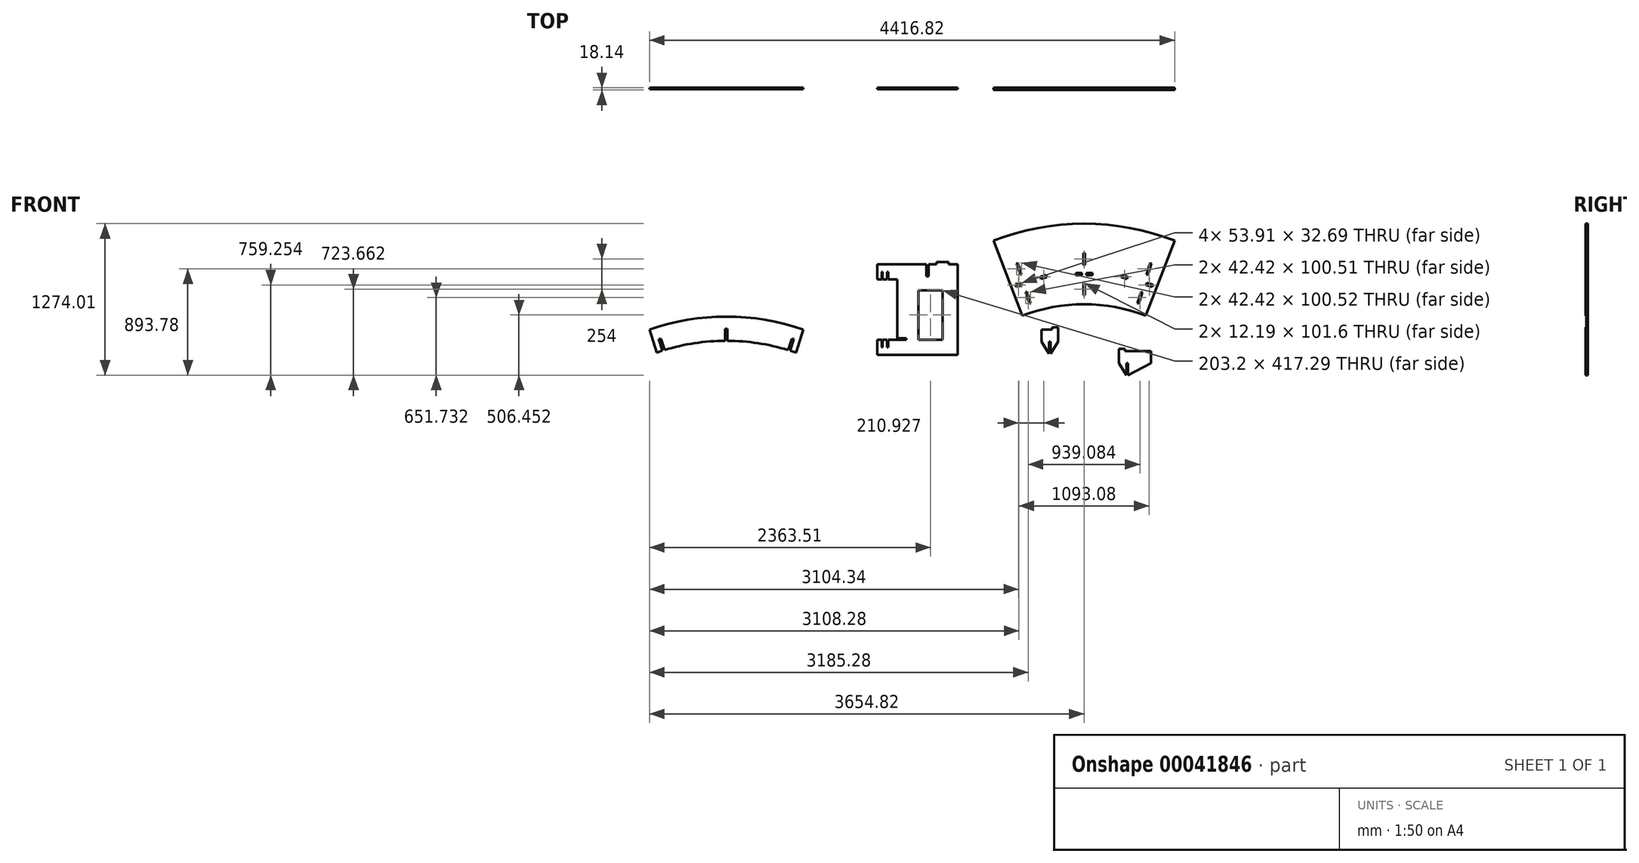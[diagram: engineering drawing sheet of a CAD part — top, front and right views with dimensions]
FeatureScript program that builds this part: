
annotation { "Feature Type Name" : "Feature", "Feature Type Description" : "" }
export const myFeature = defineFeature(function(context is Context, id is Id, definition is map)
    precondition{}
    {
        {
            var Q0;
            Q0=qCreatedBy(makeId("Front.planeOp"),FACE);
            var sketch = newSketch(context, id + "F0", { "sketchPlane" : qUnion([Q0])});
            skArc(sketch, "E0", {"start": v(822.71, 0) * mm, "mid": v(60.71, 141.8) * mm, "end": v(-701.29, 0) * mm});
            skArc(sketch, "E1.0", {"start": v(579.07, -632) * mm, "mid": v(60.71, -535.54) * mm, "end": v(-457.65, -632) * mm});
            skLineSegment(sketch, "E2", {"start": v(-701.29, 0) * mm, "end": v(-457.65, -632) * mm});
            skLineSegment(sketch, "E3", {"start": v(579.07, -632) * mm, "end": v(822.71, 0) * mm});
            skLineSegment(sketch, "E4.bottom", {"start": v(-1510, -199.4) * mm, "end": v(-1002, -199.4) * mm});
            skLineSegment(sketch, "E4.top", {"start": v(-1510, -961.4) * mm, "end": v(-1002, -961.4) * mm});
            skLineSegment(sketch, "E4.left", {"start": v(-1510, -326.4) * mm, "end": v(-1510, -822.2) * mm});
            skLineSegment(sketch, "E4.right", {"start": v(-1002, -199.4) * mm, "end": v(-1002, -961.4) * mm});
            skLineSegment(sketch, "E5.bottom", {"start": v(-1510, -199.4) * mm, "end": v(-1679.33, -199.4) * mm});
            skLineSegment(sketch, "E5.top", {"start": v(-1510, -326.4) * mm, "end": v(-1585.35, -326.4) * mm});
            skLineSegment(sketch, "E5.right", {"start": v(-1679.33, -199.4) * mm, "end": v(-1679.33, -326.4) * mm});
            skLineSegment(sketch, "E6", {"start": v(-1510, -580.4) * mm, "end": v(-1002, -580.4) * mm, "construction": true});
            skLineSegment(sketch, "E7", {"start": v(-1679.33, -262.9) * mm, "end": v(-1641.23, -262.9) * mm, "construction": true});
            skLineSegment(sketch, "E8.top", {"start": v(-1641.23, -262.9) * mm, "end": v(-1632.34, -262.9) * mm});
            skLineSegment(sketch, "E8.left", {"start": v(-1641.23, -326.4) * mm, "end": v(-1641.23, -262.9) * mm});
            skLineSegment(sketch, "E8.right", {"start": v(-1632.34, -326.4) * mm, "end": v(-1632.34, -262.9) * mm});
            skLineSegment(sketch, "E9", {"start": v(-1632.34, -262.9) * mm, "end": v(-1594.24, -262.9) * mm, "construction": true});
            skLineSegment(sketch, "E10.top", {"start": v(-1594.24, -262.9) * mm, "end": v(-1585.35, -262.9) * mm});
            skLineSegment(sketch, "E10.left", {"start": v(-1594.24, -326.4) * mm, "end": v(-1594.24, -262.9) * mm});
            skLineSegment(sketch, "E10.right", {"start": v(-1585.35, -326.4) * mm, "end": v(-1585.35, -262.9) * mm});
            skLineSegment(sketch, "E11.trimOffspring", {"start": v(-1641.23, -326.4) * mm, "end": v(-1679.33, -326.4) * mm});
            skLineSegment(sketch, "E12.trimOffspring", {"start": v(-1594.24, -326.4) * mm, "end": v(-1632.34, -326.4) * mm});
            skLineSegment(sketch, "E13.MirrorCS", {"start": v(-1641.23, -834.4) * mm, "end": v(-1679.33, -834.4) * mm});
            skLineSegment(sketch, "E14.MirrorCS", {"start": v(-1510, -834.4) * mm, "end": v(-1585.35, -834.4) * mm});
            skLineSegment(sketch, "E15.MirrorCS", {"start": v(-1632.34, -897.9) * mm, "end": v(-1594.24, -897.9) * mm, "construction": true});
            skLineSegment(sketch, "E16.MirrorCS", {"start": v(-1679.33, -897.9) * mm, "end": v(-1641.23, -897.9) * mm, "construction": true});
            skLineSegment(sketch, "E17.MirrorCS", {"start": v(-1594.24, -834.4) * mm, "end": v(-1594.24, -897.9) * mm});
            skLineSegment(sketch, "E18.MirrorCS", {"start": v(-1594.24, -834.4) * mm, "end": v(-1632.34, -834.4) * mm});
            skLineSegment(sketch, "E19.MirrorCS", {"start": v(-1679.33, -961.4) * mm, "end": v(-1679.33, -834.4) * mm});
            skLineSegment(sketch, "E20.MirrorCS", {"start": v(-1632.34, -834.4) * mm, "end": v(-1632.34, -897.9) * mm});
            skLineSegment(sketch, "E21.MirrorCS", {"start": v(-1641.23, -834.4) * mm, "end": v(-1641.23, -897.9) * mm});
            skLineSegment(sketch, "E22.MirrorCS", {"start": v(-1510, -961.4) * mm, "end": v(-1679.33, -961.4) * mm});
            skLineSegment(sketch, "E23.MirrorCS", {"start": v(-1641.23, -897.9) * mm, "end": v(-1632.34, -897.9) * mm});
            skLineSegment(sketch, "E24.MirrorCS", {"start": v(-1594.24, -897.9) * mm, "end": v(-1585.35, -897.9) * mm});
            skLineSegment(sketch, "E25.MirrorCS", {"start": v(-1585.35, -834.4) * mm, "end": v(-1585.35, -897.9) * mm});
            skLineSegment(sketch, "E26", {"start": v(-376.14, -603.35) * mm, "end": v(-581.47, 42.11) * mm, "construction": true});
            skLineSegment(sketch, "E27", {"start": v(60.71, -1976.58) * mm, "end": v(60.71, 636.15) * mm, "construction": true});
            skLineSegment(sketch, "E28", {"start": v(-476.24, -288.69) * mm, "end": v(-464.62, -285) * mm});
            skLineSegment(sketch, "E29", {"start": v(-464.62, -285) * mm, "end": v(-495.42, -188.17) * mm});
            skLineSegment(sketch, "E30", {"start": v(-495.42, -188.17) * mm, "end": v(-507.04, -191.87) * mm});
            skLineSegment(sketch, "E31", {"start": v(-507.04, -191.87) * mm, "end": v(-476.24, -288.69) * mm});
            skLineSegment(sketch, "E32.bottom", {"start": v(-1433.8, -199.4) * mm, "end": v(-1332.2, -199.4) * mm});
            skLineSegment(sketch, "E32.top", {"start": v(-1433.8, -181.26) * mm, "end": v(-1332.2, -181.26) * mm});
            skLineSegment(sketch, "E32.left", {"start": v(-1433.8, -199.4) * mm, "end": v(-1433.8, -181.26) * mm});
            skLineSegment(sketch, "E32.right", {"start": v(-1332.2, -199.4) * mm, "end": v(-1332.2, -181.26) * mm});
            skLineSegment(sketch, "E33", {"start": v(-1256, -199.4) * mm, "end": v(-1256, -961.4) * mm, "construction": true});
            skLineSegment(sketch, "E34.MirrorCS", {"start": v(-1078.2, -199.4) * mm, "end": v(-1078.2, -181.26) * mm});
            skLineSegment(sketch, "E35.MirrorCS", {"start": v(-1078.2, -199.4) * mm, "end": v(-1179.8, -199.4) * mm});
            skLineSegment(sketch, "E36.MirrorCS", {"start": v(-1179.8, -199.4) * mm, "end": v(-1179.8, -181.26) * mm});
            skLineSegment(sketch, "E37.MirrorCS", {"start": v(-1078.2, -181.26) * mm, "end": v(-1179.8, -181.26) * mm});
            skLineSegment(sketch, "E38.bottom", {"start": v(54.62, -103.75) * mm, "end": v(66.8, -103.75) * mm});
            skLineSegment(sketch, "E38.top", {"start": v(54.62, -205.35) * mm, "end": v(66.8, -205.35) * mm});
            skLineSegment(sketch, "E38.left", {"start": v(54.62, -103.75) * mm, "end": v(54.62, -205.35) * mm});
            skLineSegment(sketch, "E38.right", {"start": v(66.8, -103.75) * mm, "end": v(66.8, -205.35) * mm});
            skPoint(sketch, "E39", {"position": v(60.71, -103.75) * mm});
            skLineSegment(sketch, "E40", {"start": v(48.74, -281.55) * mm, "end": v(75.4, -281.55) * mm, "construction": true});
            skPoint(sketch, "E41.MirrorP", {"position": v(60.71, -459.35) * mm});
            skLineSegment(sketch, "E42.MirrorCS", {"start": v(54.62, -459.35) * mm, "end": v(66.8, -459.35) * mm});
            skLineSegment(sketch, "E43.MirrorCS", {"start": v(54.62, -459.35) * mm, "end": v(54.62, -357.75) * mm});
            skLineSegment(sketch, "E44.MirrorCS", {"start": v(54.62, -357.75) * mm, "end": v(66.8, -357.75) * mm});
            skLineSegment(sketch, "E45.MirrorCS", {"start": v(66.8, -459.35) * mm, "end": v(66.8, -357.75) * mm});
            skPoint(sketch, "E46", {"position": v(61.08, -535.54) * mm});
            skPoint(sketch, "E47", {"position": v(61.08, 141.8) * mm});
            skLineSegment(sketch, "E48.bottom", {"start": v(-296.1, -748.21) * mm, "end": v(-156.9, -748.21) * mm});
            skLineSegment(sketch, "E48.left", {"start": v(-296.1, -748.21) * mm, "end": v(-296.1, -849.81) * mm});
            skLineSegment(sketch, "E49.left", {"start": v(-232.6, -849.81) * mm, "end": v(-232.6, -951.41) * mm});
            skLineSegment(sketch, "E49.right", {"start": v(-220.4, -849.81) * mm, "end": v(-220.4, -951.41) * mm});
            skPoint(sketch, "E50", {"position": v(-226.5, -849.81) * mm});
            skLineSegment(sketch, "E49.bottom", {"start": v(-232.6, -849.81) * mm, "end": v(-220.4, -849.81) * mm});
            skLineSegment(sketch, "E51", {"start": v(-296.1, -849.81) * mm, "end": v(-232.6, -951.41) * mm});
            skLineSegment(sketch, "E52.left", {"start": v(-1265.07, -199.4) * mm, "end": v(-1265.07, -301) * mm});
            skPoint(sketch, "E53", {"position": v(-1256, -301) * mm});
            skLineSegment(sketch, "E52.right", {"start": v(-1246.92, -199.4) * mm, "end": v(-1246.92, -301) * mm});
            skPoint(sketch, "E54", {"position": v(-1256, -199.4) * mm});
            skLineSegment(sketch, "E52.bottom", {"start": v(-1265.07, -199.4) * mm, "end": v(-1246.92, -199.4) * mm});
            skLineSegment(sketch, "E52.top", {"start": v(-1265.07, -301) * mm, "end": v(-1246.92, -301) * mm});
            skPoint(sketch, "E55.orphan", {"position": v(-296.1, -972) * mm});
            skPoint(sketch, "E56.orphan", {"position": v(-84.24, -972) * mm});
            skLineSegment(sketch, "E57", {"start": v(-226.5, -849.81) * mm, "end": v(-226.5, -744.65) * mm, "construction": true});
            skLineSegment(sketch, "E58.MirrorCS", {"start": v(-156.9, -748.21) * mm, "end": v(-156.9, -849.81) * mm});
            skLineSegment(sketch, "E59.MirrorCS", {"start": v(-156.9, -849.81) * mm, "end": v(-220.4, -951.41) * mm});
            skLineSegment(sketch, "E60.bottom", {"start": v(-296.1, -748.21) * mm, "end": v(-245.3, -748.21) * mm});
            skLineSegment(sketch, "E60.top", {"start": v(-296.1, -730.07) * mm, "end": v(-245.3, -730.07) * mm});
            skLineSegment(sketch, "E60.left", {"start": v(-296.1, -748.21) * mm, "end": v(-296.1, -730.07) * mm});
            skLineSegment(sketch, "E60.right", {"start": v(-245.3, -748.21) * mm, "end": v(-245.3, -730.07) * mm});
            skLineSegment(sketch, "E61.MirrorCS", {"start": v(-207.7, -748.21) * mm, "end": v(-207.7, -730.07) * mm});
            skLineSegment(sketch, "E62.MirrorCS", {"start": v(-156.9, -748.21) * mm, "end": v(-156.9, -730.07) * mm});
            skLineSegment(sketch, "E63.MirrorCS", {"start": v(-156.9, -748.21) * mm, "end": v(-207.7, -748.21) * mm});
            skLineSegment(sketch, "E64.MirrorCS", {"start": v(-156.9, -730.07) * mm, "end": v(-207.7, -730.07) * mm});
            skLineSegment(sketch, "E65", {"start": v(-516.73, -372.01) * mm, "end": v(-511.23, -389.3) * mm});
            skPoint(sketch, "E66.positionSnap0", {"position": v(-513.98, -380.66) * mm});
            skLineSegment(sketch, "E67", {"start": v(-516.73, -372.01) * mm, "end": v(-468.32, -356.61) * mm});
            skLineSegment(sketch, "E68", {"start": v(-511.23, -389.3) * mm, "end": v(-462.82, -373.9) * mm});
            skLineSegment(sketch, "E69", {"start": v(-468.32, -356.61) * mm, "end": v(-462.82, -373.9) * mm});
            skPoint(sketch, "E70", {"position": v(60.79, -132.27) * mm});
            skLineSegment(sketch, "E71", {"start": v(-245.3, -739.14) * mm, "end": v(-207.7, -739.14) * mm, "construction": true});
            skPoint(sketch, "E72", {"position": v(-226.5, -739.14) * mm});
            skLineSegment(sketch, "E73.left", {"start": v(-8.88, -290.62) * mm, "end": v(-8.88, -272.48) * mm});
            skLineSegment(sketch, "E73.bottom", {"start": v(-8.88, -290.62) * mm, "end": v(41.92, -290.62) * mm});
            skLineSegment(sketch, "E73.top", {"start": v(-8.88, -272.48) * mm, "end": v(41.92, -272.48) * mm});
            skLineSegment(sketch, "E73.right", {"start": v(41.92, -290.62) * mm, "end": v(41.92, -272.48) * mm});
            skLineSegment(sketch, "E74.MirrorCS", {"start": v(130.3, -290.62) * mm, "end": v(130.3, -272.48) * mm});
            skLineSegment(sketch, "E75.MirrorCS", {"start": v(130.3, -290.62) * mm, "end": v(79.5, -290.62) * mm});
            skLineSegment(sketch, "E76.MirrorCS", {"start": v(79.5, -290.62) * mm, "end": v(79.5, -272.48) * mm});
            skLineSegment(sketch, "E77.MirrorCS", {"start": v(130.3, -272.48) * mm, "end": v(79.5, -272.48) * mm});
            skPoint(sketch, "E78", {"position": v(41.92, -281.55) * mm});
            skLineSegment(sketch, "E79", {"start": v(41.92, -281.55) * mm, "end": v(48.74, -281.55) * mm, "construction": true});
            skLineSegment(sketch, "E80", {"start": v(-465.57, -365.26) * mm, "end": v(-303.05, -313.56) * mm, "construction": true});
            skLineSegment(sketch, "E81.MirrorCS", {"start": v(-430.04, -433.92) * mm, "end": v(-418.42, -430.22) * mm});
            skLineSegment(sketch, "E82.MirrorCS", {"start": v(-387.62, -527.04) * mm, "end": v(-399.24, -530.74) * mm});
            skLineSegment(sketch, "E83.MirrorCS", {"start": v(-399.24, -530.74) * mm, "end": v(-430.04, -433.92) * mm});
            skLineSegment(sketch, "E84.MirrorCS", {"start": v(-418.42, -430.22) * mm, "end": v(-387.62, -527.04) * mm});
            skLineSegment(sketch, "E85.MirrorCS", {"start": v(597.66, -288.69) * mm, "end": v(586.04, -285) * mm});
            skLineSegment(sketch, "E86.MirrorCS", {"start": v(616.84, -188.17) * mm, "end": v(628.46, -191.87) * mm});
            skLineSegment(sketch, "E87.MirrorCS", {"start": v(586.04, -285) * mm, "end": v(616.84, -188.17) * mm});
            skLineSegment(sketch, "E88.MirrorCS", {"start": v(628.46, -191.87) * mm, "end": v(597.66, -288.69) * mm});
            skLineSegment(sketch, "E89.MirrorCS", {"start": v(551.46, -433.92) * mm, "end": v(539.84, -430.22) * mm});
            skLineSegment(sketch, "E90.MirrorCS", {"start": v(509.04, -527.04) * mm, "end": v(520.66, -530.74) * mm});
            skLineSegment(sketch, "E91.MirrorCS", {"start": v(520.66, -530.74) * mm, "end": v(551.46, -433.92) * mm});
            skLineSegment(sketch, "E92.MirrorCS", {"start": v(539.84, -430.22) * mm, "end": v(509.04, -527.04) * mm});
            skLineSegment(sketch, "E93.MirrorCS", {"start": v(638.15, -372.01) * mm, "end": v(632.65, -389.3) * mm});
            skLineSegment(sketch, "E94.MirrorCS", {"start": v(589.74, -356.61) * mm, "end": v(584.24, -373.9) * mm});
            skPoint(sketch, "E95.MirrorP", {"position": v(635.4, -380.66) * mm});
            skLineSegment(sketch, "E96.MirrorCS", {"start": v(632.65, -389.3) * mm, "end": v(584.24, -373.9) * mm});
            skLineSegment(sketch, "E97.MirrorCS", {"start": v(638.15, -372.01) * mm, "end": v(589.74, -356.61) * mm});
            skLineSegment(sketch, "E98", {"start": v(-384.31, -339.4) * mm, "end": v(-444.42, -150.46) * mm, "construction": true});
            skPoint(sketch, "E99.MirrorP", {"position": v(-254.64, -298.16) * mm});
            skLineSegment(sketch, "E100.MirrorCS", {"start": v(-305.8, -304.91) * mm, "end": v(-300.3, -322.2) * mm});
            skLineSegment(sketch, "E101.MirrorCS", {"start": v(-257.4, -289.51) * mm, "end": v(-251.9, -306.8) * mm});
            skLineSegment(sketch, "E102.MirrorCS", {"start": v(-257.4, -289.51) * mm, "end": v(-305.8, -304.91) * mm});
            skLineSegment(sketch, "E103.MirrorCS", {"start": v(-251.9, -306.8) * mm, "end": v(-300.3, -322.2) * mm});
            skLineSegment(sketch, "E104.MirrorCS", {"start": v(378.81, -289.51) * mm, "end": v(373.31, -306.8) * mm});
            skPoint(sketch, "E105.MirrorP", {"position": v(376.06, -298.16) * mm});
            skLineSegment(sketch, "E106.MirrorCS", {"start": v(373.31, -306.8) * mm, "end": v(421.72, -322.2) * mm});
            skLineSegment(sketch, "E107.MirrorCS", {"start": v(427.22, -304.91) * mm, "end": v(421.72, -322.2) * mm});
            skLineSegment(sketch, "E108.MirrorCS", {"start": v(378.81, -289.51) * mm, "end": v(427.22, -304.91) * mm});
            skLineSegment(sketch, "E109", {"start": v(-1299.86, -199.4) * mm, "end": v(-1299.86, -417.12) * mm, "construction": true});
            skLineSegment(sketch, "E110", {"start": v(-1002, -510.07) * mm, "end": v(-1129, -510.07) * mm, "construction": true});
            skLineSegment(sketch, "E111", {"start": v(-1319.66, -961.4) * mm, "end": v(-1319.66, -834.4) * mm, "construction": true});
            skLineSegment(sketch, "E112.bottom", {"start": v(-1332.2, -417.12) * mm, "end": v(-1129, -417.12) * mm});
            skLineSegment(sketch, "E112.top", {"start": v(-1332.2, -834.4) * mm, "end": v(-1129, -834.4) * mm});
            skLineSegment(sketch, "E112.left", {"start": v(-1332.2, -417.12) * mm, "end": v(-1332.2, -834.4) * mm});
            skLineSegment(sketch, "E112.right", {"start": v(-1129, -417.12) * mm, "end": v(-1129, -834.4) * mm});
            skLineSegment(sketch, "E113.left", {"start": v(-1332.2, -834.4) * mm, "end": v(-1332.2, -815.86) * mm});
            skLineSegment(sketch, "E113.right", {"start": v(-1433.8, -834.4) * mm, "end": v(-1433.8, -822.2) * mm});
            skPoint(sketch, "E114", {"position": v(489.26, -919.94) * mm});
            skLineSegment(sketch, "E115.bottom", {"start": v(353.19, -929) * mm, "end": v(625.33, -929) * mm});
            skPoint(sketch, "E116", {"position": v(422.78, -1030.6) * mm});
            skLineSegment(sketch, "E115.left", {"start": v(353.19, -929) * mm, "end": v(353.19, -1030.6) * mm});
            skLineSegment(sketch, "E117.MirrorCS", {"start": v(625.33, -929) * mm, "end": v(574.53, -929) * mm});
            skLineSegment(sketch, "E118.right", {"start": v(428.88, -1030.6) * mm, "end": v(428.88, -1132.2) * mm});
            skLineSegment(sketch, "E118.left", {"start": v(416.69, -1030.6) * mm, "end": v(416.69, -1132.2) * mm});
            skPoint(sketch, "E119.orphan", {"position": v(514.52, -1119.3) * mm});
            skLineSegment(sketch, "E120.MirrorCS", {"start": v(625.33, -910.87) * mm, "end": v(574.53, -910.87) * mm});
            skLineSegment(sketch, "E121.MirrorCS", {"start": v(625.33, -929) * mm, "end": v(625.33, -1030.6) * mm});
            skLineSegment(sketch, "E122", {"start": v(353.19, -1030.6) * mm, "end": v(416.69, -1132.2) * mm});
            skLineSegment(sketch, "E123.top", {"start": v(353.19, -910.87) * mm, "end": v(403.99, -910.87) * mm});
            skPoint(sketch, "E124.orphan", {"position": v(353.19, -1119.3) * mm});
            skLineSegment(sketch, "E125.MirrorCS", {"start": v(625.33, -1030.6) * mm, "end": v(428.88, -1132.2) * mm});
            skLineSegment(sketch, "E123.bottom", {"start": v(353.19, -929) * mm, "end": v(403.99, -929) * mm});
            skLineSegment(sketch, "E126", {"start": v(403.99, -919.94) * mm, "end": v(574.53, -919.94) * mm, "construction": true});
            skLineSegment(sketch, "E123.right", {"start": v(403.99, -929) * mm, "end": v(403.99, -910.87) * mm});
            skLineSegment(sketch, "E127.MirrorCS", {"start": v(574.53, -929) * mm, "end": v(574.53, -910.87) * mm});
            skLineSegment(sketch, "E118.bottom", {"start": v(416.69, -1030.6) * mm, "end": v(428.88, -1030.6) * mm});
            skLineSegment(sketch, "E123.left", {"start": v(353.19, -929) * mm, "end": v(353.19, -910.87) * mm});
            skLineSegment(sketch, "E128.MirrorCS", {"start": v(625.33, -929) * mm, "end": v(625.33, -910.87) * mm});
            skLineSegment(sketch, "E129.MirrorCS", {"start": v(1775.37, -902.65) * mm, "end": v(1775.39, -902.65) * mm});
            skLineSegment(sketch, "E130", {"start": v(-1433.8, -822.2) * mm, "end": v(-1510, -822.2) * mm});
            skLineSegment(sketch, "E131", {"start": v(-1433.8, -834.4) * mm, "end": v(-1510, -834.4) * mm});
            skPoint(sketch, "E132", {"position": v(-2969.11, -919.18) * mm});
            skPoint(sketch, "E133", {"position": v(-2947.27, -769.9) * mm});
            skPoint(sketch, "E134", {"position": v(-2947.34, -741.38) * mm});
            skLineSegment(sketch, "E135.right", {"start": v(-2938.27, -741.38) * mm, "end": v(-2938.27, -842.98) * mm});
            skLineSegment(sketch, "E135.left", {"start": v(-2956.41, -741.38) * mm, "end": v(-2956.41, -842.98) * mm});
            skLineSegment(sketch, "E136", {"start": v(-3497.8, -824) * mm, "end": v(-3515.1, -829.5) * mm});
            skLineSegment(sketch, "E137.MirrorCS", {"start": v(-2396.88, -824) * mm, "end": v(-2379.6, -829.5) * mm});
            skLineSegment(sketch, "E135.top", {"start": v(-2956.41, -842.98) * mm, "end": v(-2956.16, -842.98) * mm});
            skLineSegment(sketch, "E135.bottom", {"start": v(-2956.41, -741.38) * mm, "end": v(-2938.27, -741.38) * mm});
            skLineSegment(sketch, "E138", {"start": v(-3515.1, -829.5) * mm, "end": v(-3484.3, -926.31) * mm});
            skLineSegment(sketch, "E139", {"start": v(-3467, -920.81) * mm, "end": v(-3497.8, -824) * mm});
            skLineSegment(sketch, "E140.MirrorCS", {"start": v(-2379.6, -829.5) * mm, "end": v(-2410.4, -926.31) * mm});
            skLineSegment(sketch, "E141.MirrorCS", {"start": v(-2427.68, -920.81) * mm, "end": v(-2396.88, -824) * mm});
            skArc(sketch, "E142.0", {"start": v(-2300.58, -748.7) * mm, "mid": v(-2947.34, -639.76) * mm, "end": v(-3594.1, -748.7) * mm});
            skArc(sketch, "E143.0", {"start": v(-2362.2, -942.4) * mm, "mid": v(-2386.24, -934.18) * mm, "end": v(-2410.4, -926.31) * mm});
            skArc(sketch, "E144.trimOffspring", {"start": v(-2956.16, -842.98) * mm, "mid": v(-3214.43, -863.21) * mm, "end": v(-3466.98, -920.9) * mm});
            skLineSegment(sketch, "E145.trimOffspring", {"start": v(-2938.52, -842.98) * mm, "end": v(-2938.27, -842.98) * mm});
            skLineSegment(sketch, "E146", {"start": v(-3467, -920.81) * mm, "end": v(-3466.98, -920.9) * mm});
            skLineSegment(sketch, "E147", {"start": v(-2427.68, -920.81) * mm, "end": v(-2427.7, -920.9) * mm});
            skArc(sketch, "E148.trimOffspring", {"start": v(-2427.7, -920.9) * mm, "mid": v(-2680.26, -863.21) * mm, "end": v(-2938.52, -842.98) * mm});
            skArc(sketch, "E149.trimOffspring", {"start": v(-3484.3, -926.31) * mm, "mid": v(-3508.45, -934.18) * mm, "end": v(-3532.48, -942.4) * mm});
            skLineSegment(sketch, "E150", {"start": v(-3532.48, -942.4) * mm, "end": v(-3594.1, -748.7) * mm});
            skLineSegment(sketch, "E151", {"start": v(-2947.27, -769.9) * mm, "end": v(-2947.34, -741.38) * mm, "construction": true});
            skLineSegment(sketch, "E152.0", {"start": v(-2331.18, -844.9) * mm, "end": v(-2361.98, -941.71) * mm});
            skLineSegment(sketch, "E153", {"start": v(-2361.98, -941.71) * mm, "end": v(-2362.2, -942.4) * mm});
            skLineSegment(sketch, "E154", {"start": v(-2331.18, -844.9) * mm, "end": v(-2300.58, -748.7) * mm});
            skLineSegment(sketch, "E155", {"start": v(-840.28, 210.13) * mm, "end": v(-840.5, 209.44) * mm});
            skSolve(sketch);
        }
        {
            var Q0;
            Q0=makeQuery(id+"F0.imprint","IMPRINT",FACE,{"disambiguationData":[TD([[makeQuery(id+"F0.imprint","IMPRINT",EDGE,{"derivedFrom":sQuery(id+"F0.wireOp",EDGE,"E48.bottom")}),-1.0]])]});
            var Q1;
            Q1=makeQuery(id+"F0.imprint","IMPRINT",FACE,{"disambiguationData":[TD([[makeQuery(id+"F0.imprint","IMPRINT",EDGE,{"derivedFrom":sQuery(id+"F0.wireOp",EDGE,"E61.MirrorCS")}),-1.0]])]});
            var Q2;
            Q2=makeQuery(id+"F0.imprint","IMPRINT",FACE,{"disambiguationData":[TD([[makeQuery(id+"F0.imprint","IMPRINT",EDGE,{"derivedFrom":sQuery(id+"F0.wireOp",EDGE,"E60.bottom")}),1.0]])]});
            var Q3;
            Q3=makeQuery(id+"F0.imprint","IMPRINT",FACE,{"disambiguationData":[TD([[makeQuery(id+"F0.imprint","IMPRINT",EDGE,{"derivedFrom":sQuery(id+"F0.wireOp",EDGE,"E0")}),1.0]])]});
            var Q4;
            Q4=makeQuery(id+"F0.imprint","IMPRINT",FACE,{"disambiguationData":[TD([[makeQuery(id+"F0.imprint","IMPRINT",EDGE,{"derivedFrom":sQuery(id+"F0.wireOp",EDGE,"E123.top")}),-1.0]])]});
            var Q5;
            Q5=makeQuery(id+"F0.imprint","IMPRINT",FACE,{"disambiguationData":[TD([[makeQuery(id+"F0.imprint","IMPRINT",EDGE,{"derivedFrom":sQuery(id+"F0.wireOp",EDGE,"E115.bottom")}),-1.0]])]});
            var Q6;
            Q6=makeQuery(id+"F0.imprint","IMPRINT",FACE,{"disambiguationData":[TD([[makeQuery(id+"F0.imprint","IMPRINT",EDGE,{"derivedFrom":sQuery(id+"F0.wireOp",EDGE,"E117.MirrorCS")}),-1.0]])]});
            var Q7;
            {var subQ11=sQuery(id+"F0.wireOp",EDGE,"4b4208f6-c2fb-4491-82b5-bbb72651a30f");Q7=makeQuery(id+"F0.imprint","IMPRINT",FACE,{"disambiguationData":[TD([[makeQuery(id+"F0.imprint","IMPRINT",EDGE,{"derivedFrom":subQ11}),1.0]])]});}
            var Q8;
            Q8=makeQuery(id+"F0.imprint","IMPRINT",FACE,{"disambiguationData":[TD([[makeQuery(id+"F0.imprint","IMPRINT",EDGE,{"derivedFrom":sQuery(id+"F0.wireOp",EDGE,"ZEEkujvX-f0nl-X2ht-5uEe-wjA7yF6qMzgc")}),1.0]])]});
            var Q9;
            {var subQ0=sQuery(id+"F0.wireOp",EDGE,"cHDWE3Ce-WObb-T2iv-pb7J-tTBgFW9YY9rB");Q9=makeQuery(id+"F0.imprint","IMPRINT",FACE,{"disambiguationData":[TD([[makeQuery(id+"F0.imprint","IMPRINT",EDGE,{"derivedFrom":subQ0}),-1.0]])]});}
            var Q10;
            Q10=makeQuery(id+"F0.imprint","IMPRINT",FACE,{"disambiguationData":[TD([[makeQuery(id+"F0.imprint","IMPRINT",EDGE,{"derivedFrom":sQuery(id+"F0.wireOp",EDGE,"80414a30-6be5-4261-b871-3fd237e30337.0")}),1.0]])]});
            extrude(context, id + "F1", {"entities" : qUnion([Q0, Q1, Q2, Q3, Q4, Q5, Q6, Q7, Q8, Q9, Q10]), "depth" : 18.14 * mm});
        }
        {
            var Q0;
            Q0=makeQuery(id+"F0.imprint","IMPRINT",FACE,{"disambiguationData":[TD([[makeQuery(id+"F0.imprint","IMPRINT",EDGE,{"derivedFrom":sQuery(id+"F0.wireOp",EDGE,"E135.right")}),1.0]])]});
            var Q1;
            Q1=makeQuery(id+"F0.imprint","IMPRINT",FACE,{"disambiguationData":[TD([[makeQuery(id+"F0.imprint","IMPRINT",EDGE,{"derivedFrom":sQuery(id+"F0.wireOp",EDGE,"E4.top")}),1.0]])]});
            var Q2;
            Q2=makeQuery(id+"F0.imprint","IMPRINT",FACE,{"disambiguationData":[TD([[makeQuery(id+"F0.imprint","IMPRINT",EDGE,{"derivedFrom":sQuery(id+"F0.wireOp",EDGE,"E32.bottom")}),1.0]])]});
            var Q3;
            Q3=makeQuery(id+"F0.imprint","IMPRINT",FACE,{"disambiguationData":[TD([[makeQuery(id+"F0.imprint","IMPRINT",EDGE,{"derivedFrom":sQuery(id+"F0.wireOp",EDGE,"E34.MirrorCS")}),1.0]])]});
            extrude(context, id + "F2", {"entities" : qUnion([Q0, Q1, Q2, Q3]), "depth" : 12.2 * mm});
        }
    });
